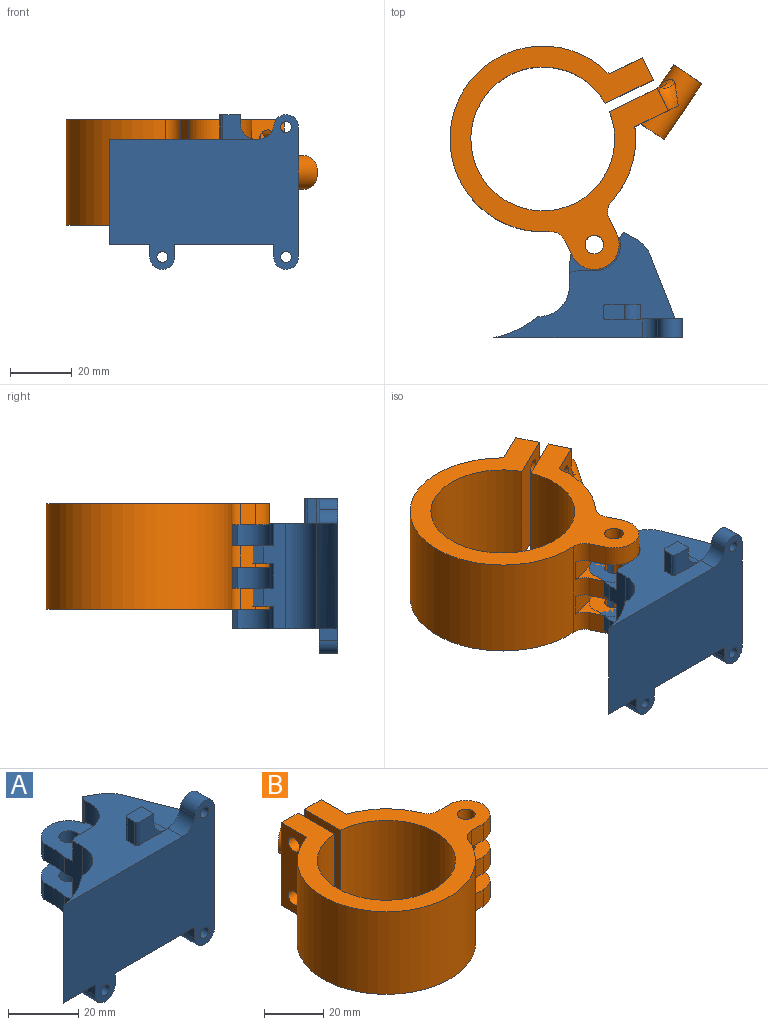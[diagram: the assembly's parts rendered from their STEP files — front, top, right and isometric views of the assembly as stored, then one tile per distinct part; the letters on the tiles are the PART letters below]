
ASSEMBLY  parts=2 mates=1
PART A: 57 faces, bbox 63x38x50 mm
  f0: plane 8.93x6mm, normal (1,0,0), area 36.2mm2, adj f1,f3,f4,f56
  f1: cylinder r=4mm len=7.98mm, axis (0,-1,0), area 73.1mm2, adj f0,f3,f4,f55
  f2: cylinder r=1.75mm len=6mm, axis (0,-1,0), area 66mm2, adj f3,f4
  f3: plane 13x12.94mm, normal (0,1,0), area 57.5mm2, adj f0,f1,f2,f5,f15,f55,f56
  f4: plane 60.96x50mm, normal (0,-1,0), area 2220.3mm2, adj f0,f1,f2,f5,f6,f7,f15,f31
  f5: plane 58.61x34.05mm, normal (0,0,1), area 807.8mm2, adj f3,f4,f8,f13,f14,f15,f18,f19
  f6: plane 45.29x34.05mm, normal (0,0,-1), area 818.7mm2, adj f4,f8,f13,f14,f15,f18,f19,f21
  f7: plane 12.96x5.72mm, normal (0,0,-1), area 29.2mm2, adj f4,f31,f41
  f8: plane 34x4.24mm, normal (0.48,0.88,0), area 164.1mm2, adj f5,f6,f14,f34
  f9: plane 17.26x16.5mm, normal (0,0,1), area 195mm2, adj f17,f18,f20,f24,f29,f30,f33,f34
  f10: plane 17.26x16.5mm, normal (0,0,-1), area 195mm2, adj f17,f18,f21,f22,f23,f24,f33,f34
  f11: plane 17.26x16.5mm, normal (0,0,1), area 195mm2, adj f16,f18,f25,f26,f27,f28,f32,f34
  f12: plane 17.26x16.5mm, normal (0,0,-1), area 195mm2, adj f16,f18,f20,f28,f29,f30,f32,f34
  f13: cylinder r=10mm len=34mm, axis (0,0,1), area 534.1mm2, adj f5,f6,f18,f19
  f14: cylinder r=10mm len=34mm, axis (0,0,1), area 238.2mm2, adj f5,f6,f8,f15
  f15: plane 34x26.6mm, normal (0.93,0.36,0), area 938.9mm2, adj f3,f4,f5,f6,f14,f35,f56
  f16: cylinder r=8mm len=15.35mm, axis (0,0,1), area 120.2mm2, adj f11,f12,f28,f34
  f17: cylinder r=8mm len=15.35mm, axis (0,0,1), area 120.2mm2, adj f9,f10,f24,f34
  f18: plane 34x7.19mm, normal (-1,0,0), area 172.9mm2, adj f5,f6,f9,f10,f11,f12,f13,f23
  f19: plane 34x0.26mm, normal (0,1,0), area 8.8mm2, adj f5,f6,f13,f31
  f20: plane 7.8x5.5mm, normal (0,1,0), area 42.9mm2, adj f9,f12,f29,f30
  f21: cylinder r=8.5mm len=10.73mm, axis (0,0,-1), area 113.9mm2, adj f6,f10,f22,f34
  f22: plane 7.3x5.5mm, normal (0,1,0), area 40.2mm2, adj f6,f10,f21,f23
  f23: cylinder r=4.5mm len=7.3mm, axis (0,0,-1), area 19.3mm2, adj f6,f10,f18,f22
  f24: cylinder r=30.61mm len=8.8mm, axis (0,0,-1), area 51.3mm2, adj f9,f10,f17,f18
  f25: cylinder r=8.5mm len=10.73mm, axis (0,0,-1), area 113.9mm2, adj f5,f11,f26,f34
  f26: plane 7.3x5.5mm, normal (0,1,0), area 40.2mm2, adj f5,f11,f25,f27
  f27: cylinder r=4.5mm len=7.3mm, axis (0,0,-1), area 19.3mm2, adj f5,f11,f18,f26
  f28: cylinder r=30.61mm len=8.8mm, axis (0,0,-1), area 51.3mm2, adj f11,f12,f16,f18
  f29: cylinder r=4.5mm len=7.8mm, axis (0,0,-1), area 20.6mm2, adj f9,f12,f18,f20
  f30: cylinder r=8.5mm len=10.73mm, axis (0,0,-1), area 121.7mm2, adj f9,f12,f20,f34
  f31: cylinder r=30.5mm len=34mm, axis (0,0,-1), area 542mm2, adj f4,f5,f6,f7,f19,f44
  f32: cylinder r=3mm len=6mm, axis (0,0,1), area 109.3mm2, adj f11,f12
  f33: cylinder r=3mm len=6mm, axis (0,0,1), area 109.3mm2, adj f9,f10
  f34: plane 34x2.44mm, normal (-0.86,0.51,0), area 80.1mm2, adj f5,f6,f8,f9,f10,f11,f12,f16
  f35: plane 6x2.35mm, normal (0,0,1), area 7mm2, adj f15,f38,f40
  f36: plane 6x4mm, normal (-1,0,0), area 24mm2, adj f4,f6,f37,f40
  f37: cylinder r=4mm len=8mm, axis (0,-1,0), area 75.8mm2, adj f4,f36,f38,f40
  f38: plane 6x3.93mm, normal (1,0,0), area 23.6mm2, adj f4,f35,f37,f40
  f39: cylinder r=1.75mm len=6mm, axis (0,-1,0), area 66mm2, adj f4,f40
  f40: plane 8x8mm, normal (0,1,0), area 47.5mm2, adj f6,f35,f36,f37,f38,f39
  f41: plane 6x4mm, normal (-1,0,0), area 24mm2, adj f4,f7,f42,f44,f46
  f42: cylinder r=4mm len=8mm, axis (0,-1,0), area 75.4mm2, adj f4,f41,f43,f46
  f43: plane 6x4mm, normal (1,0,0), area 24mm2, adj f4,f6,f42,f46
  f44: plane 0.36x0.28mm, normal (0,0,1), area 0.1mm2, adj f31,f41,f46
  f45: cylinder r=1.75mm len=6mm, axis (0,-1,0), area 66mm2, adj f4,f46
  f46: plane 8x8mm, normal (0,1,0), area 47.5mm2, adj f6,f41,f42,f43,f44,f45
  f47: plane 10.76x8mm, normal (0,1,0), area 51.4mm2, adj f5,f50,f51,f52,f54
  f48: plane 8x3mm, normal (-1,0,0), area 24mm2, adj f5,f51,f52,f53
  f49: plane 10.76x8mm, normal (0,-1,0), area 51.4mm2, adj f5,f50,f51,f53,f54
  f50: plane 5x3mm, normal (1,0,0), area 15mm2, adj f47,f49,f51,f54
  f51: plane 6.76x5mm, normal (0,0,1), area 33.4mm2, adj f47,f48,f49,f50,f52,f53
  f52: cylinder r=1mm len=8mm, axis (0,0,1), area 12.6mm2, adj f5,f47,f48,f51
  f53: cylinder r=1mm len=8mm, axis (0,0,1), area 12.6mm2, adj f5,f48,f49,f51
  f54: cylinder r=5mm len=5mm, axis (0,1,0), area 39.3mm2, adj f5,f47,f49,f50
  f55: cylinder r=5mm len=6mm, axis (0,-1,0), area 43.8mm2, adj f1,f3,f4,f5
  f56: cylinder r=5mm len=6.8mm, axis (-0.36,0.93,0), area 20.6mm2, adj f0,f3,f15
PART B: 48 faces, bbox 77.8x85.8x35.8 mm
  f0: bspline ~14.84x5.11mm, area 31.4mm2, adj f1,f15,f38,f46
  f1: bspline ~6.56x5.87mm, area 12.8mm2, adj f0,f15,f38,f45
  f2: plane 8x7.21mm, normal (0,1,0), area 53.6mm2, adj f4,f15,f26,f47
  f3: plane 16.11x14.66mm, normal (1,0,0), area 125.1mm2, adj f14,f24,f27,f36,f38,f43,f45
  f4: plane 16.11x14.66mm, normal (1,0,0), area 125.1mm2, adj f2,f24,f26,f36,f38,f44,f47
  f5: cylinder r=5mm len=34mm, axis (0,0,-1), area 134.4mm2, adj f6,f7,f20,f21,f26,f27,f28,f29
  f6: plane 6.8x5.5mm, normal (0,-1,0), area 37.4mm2, adj f5,f8,f29,f31
  f7: plane 6.8x5.5mm, normal (0,-1,0), area 37.4mm2, adj f5,f9,f27,f28
  f8: cylinder r=8mm len=16mm, axis (0,0,-1), area 170.9mm2, adj f6,f10,f29,f31
  f9: cylinder r=8mm len=16mm, axis (0,0,-1), area 170.9mm2, adj f7,f11,f27,f28
  f10: plane 6.8x5.5mm, normal (0,1,0), area 37.4mm2, adj f8,f12,f29,f31
  f11: plane 6.8x5.5mm, normal (0,1,0), area 37.4mm2, adj f9,f12,f27,f28
  f12: cylinder r=5mm len=34mm, axis (0,0,-1), area 134.4mm2, adj f10,f11,f23,f24,f26,f27,f28,f29
  f13: cylinder r=3mm len=6.8mm, axis (0,0,-1), area 128.2mm2, adj f27,f28
  f14: plane 8x7.21mm, normal (0,1,0), area 53.6mm2, adj f3,f15,f27,f45
  f15: plane 35.8x19.05mm, normal (-1,0,0), area 539.1mm2, adj f0,f1,f2,f14,f16,f26,f27,f43
  f16: cylinder r=23.25mm len=46.5mm, axis (0,0,-1), area 4864.8mm2, adj f15,f17,f26,f27
  f17: plane 34x17.25mm, normal (1,0,0), area 539.1mm2, adj f16,f18,f26,f27,f41,f42
  f18: plane 34x8mm, normal (0,1,0), area 272mm2, adj f17,f19,f26,f27
  f19: plane 34x12mm, normal (-1,0,0), area 360.5mm2, adj f18,f20,f26,f27,f41,f42
  f20: cylinder r=30mm len=58.46mm, axis (0,0,-1), area 4089.8mm2, adj f5,f19,f26,f27
  f21: plane 6.8x5.5mm, normal (0,-1,0), area 37.4mm2, adj f5,f22,f26,f32
  f22: cylinder r=8mm len=16mm, axis (0,0,-1), area 170.9mm2, adj f21,f23,f26,f32
  f23: plane 6.8x5.5mm, normal (0,1,0), area 37.4mm2, adj f12,f22,f26,f32
  f24: cylinder r=30mm len=34mm, axis (0,0,-1), area 872.9mm2, adj f3,f4,f12,f26,f27,f35,f36
  f25: cylinder r=3mm len=6.8mm, axis (0,0,-1), area 128.2mm2, adj f26,f32
  f26: plane 76x70.46mm, normal (0,0,1), area 1496.4mm2, adj f2,f4,f5,f12,f15,f16,f17,f18
  f27: plane 76x70.46mm, normal (0,0,-1), area 1496.4mm2, adj f3,f5,f7,f9,f11,f12,f13,f14
  f28: plane 20.59x17.71mm, normal (0,0,1), area 208.2mm2, adj f5,f7,f9,f11,f12,f13,f30
  f29: plane 20.59x17.71mm, normal (0,0,-1), area 208.2mm2, adj f5,f6,f8,f10,f12,f30,f34
  f30: cylinder r=30.11mm len=20.59mm, axis (0,0,-1), area 142.9mm2, adj f5,f12,f28,f29
  f31: plane 20.59x17.71mm, normal (0,0,1), area 208.2mm2, adj f5,f6,f8,f10,f12,f33,f34
  f32: plane 20.59x17.71mm, normal (0,0,-1), area 208.2mm2, adj f5,f12,f21,f22,f23,f25,f33
  f33: cylinder r=30.11mm len=20.59mm, axis (0,0,-1), area 142.9mm2, adj f5,f12,f31,f32
  f34: cylinder r=3mm len=6.8mm, axis (0,0,-1), area 128.2mm2, adj f29,f31
  f35: plane 8.37x1.67mm, normal (-0.5,0.87,0), area 11.2mm2, adj f24,f36
  f36: cylinder r=5.5mm len=8.37mm, axis (0.5,-0.87,0), area 24.7mm2, adj f3,f4,f24,f35,f37
  f37: plane 11x9.53mm, normal (0.5,-0.87,0), area 61.9mm2, adj f36,f38,f40
  f38: cylinder r=5.5mm len=24.38mm, axis (-0.5,0.87,0), area 474.1mm2, adj f0,f1,f3,f4,f37,f39,f45,f46
  f39: plane 11x9.53mm, normal (-0.5,0.87,0), area 61.9mm2, adj f38,f40
  f40: cylinder r=3.25mm len=22.13mm, axis (-0.5,0.87,0), area 445.2mm2, adj f37,f39
  f41: cylinder r=2.75mm len=8mm, axis (-1,0,0), area 138.2mm2, adj f17,f19
  f42: cylinder r=2.75mm len=8mm, axis (-1,0,0), area 138.2mm2, adj f17,f19
  f43: cylinder r=2.75mm len=8mm, axis (-1,0,0), area 138.2mm2, adj f3,f15
  f44: cylinder r=2.75mm len=8mm, axis (-1,0,0), area 138.2mm2, adj f4,f15
  f45: bspline ~10.44x5.95mm, area 55.1mm2, adj f1,f3,f14,f38
  f46: bspline ~6.55x5.86mm, area 12.7mm2, adj f0,f15,f38,f47
  f47: bspline ~10.44x5.95mm, area 55.1mm2, adj f2,f4,f38,f46
PLACE A t=(-39.99,21.39,-2.58)mm fixed
PLACE B rot(axis=(0,0,-1),64deg) t=(-18.64,55.54,3.72)mm
MATE revolute B.f13 <-> A.f32  axis (0,0,1) through (-1.99,21.39,24.12)mm
